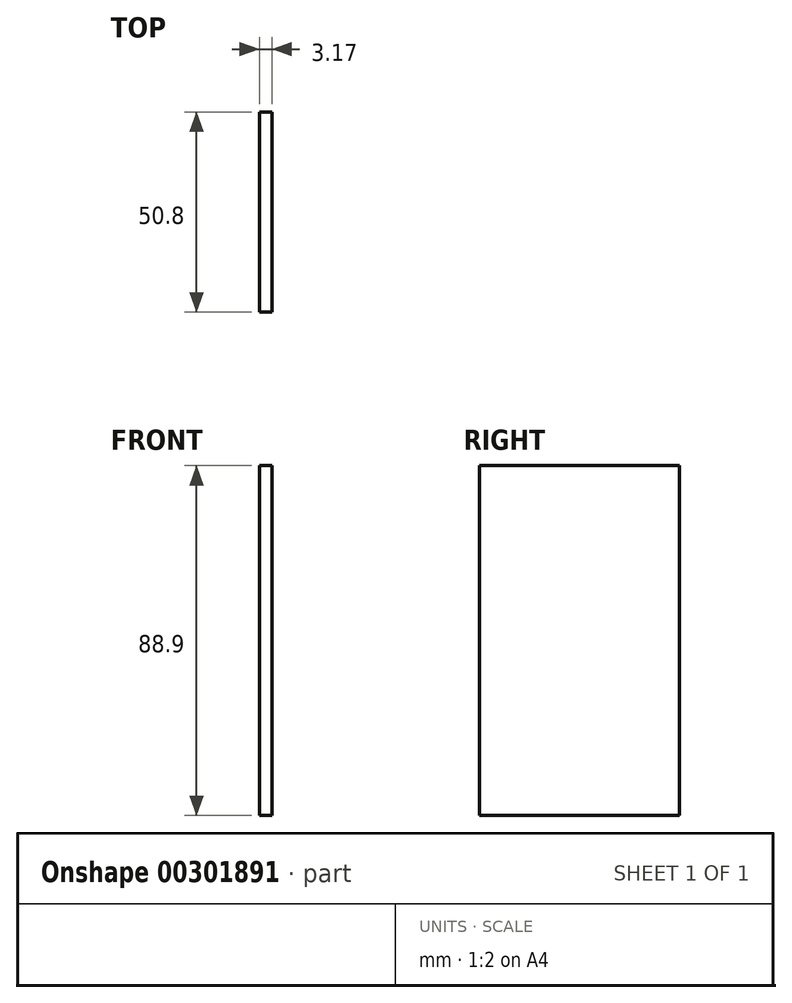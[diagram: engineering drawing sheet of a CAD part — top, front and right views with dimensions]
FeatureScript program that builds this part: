
annotation { "Feature Type Name" : "Feature", "Feature Type Description" : "" }
export const myFeature = defineFeature(function(context is Context, id is Id, definition is map)
    precondition{}
    {
        {
            var Q0;
            Q0=qCreatedBy(makeId("Right.planeOp"),FACE);
            var sketch = newSketch(context, id + "F0", { "sketchPlane" : qUnion([Q0])});
            skLineSegment(sketch, "E0.bottom", {"start": v(-25.4, -44.45) * mm, "end": v(25.4, -44.45) * mm});
            skLineSegment(sketch, "E0.top", {"start": v(-25.4, 44.45) * mm, "end": v(25.4, 44.45) * mm});
            skLineSegment(sketch, "E0.left", {"start": v(-25.4, -44.45) * mm, "end": v(-25.4, 44.45) * mm});
            skLineSegment(sketch, "E0.right", {"start": v(25.4, -44.45) * mm, "end": v(25.4, 44.45) * mm});
            skPoint(sketch, "E0.middle", {"position": v(0, 0) * mm});
            skSolve(sketch);
        }
        {
            var Q0;
            Q0 = qSketchRegion(id + "F0", true);
            extrude(context, id + "F1", {"entities" : qUnion([Q0]), "depth" : 3.17 * mm});
        }
    });
